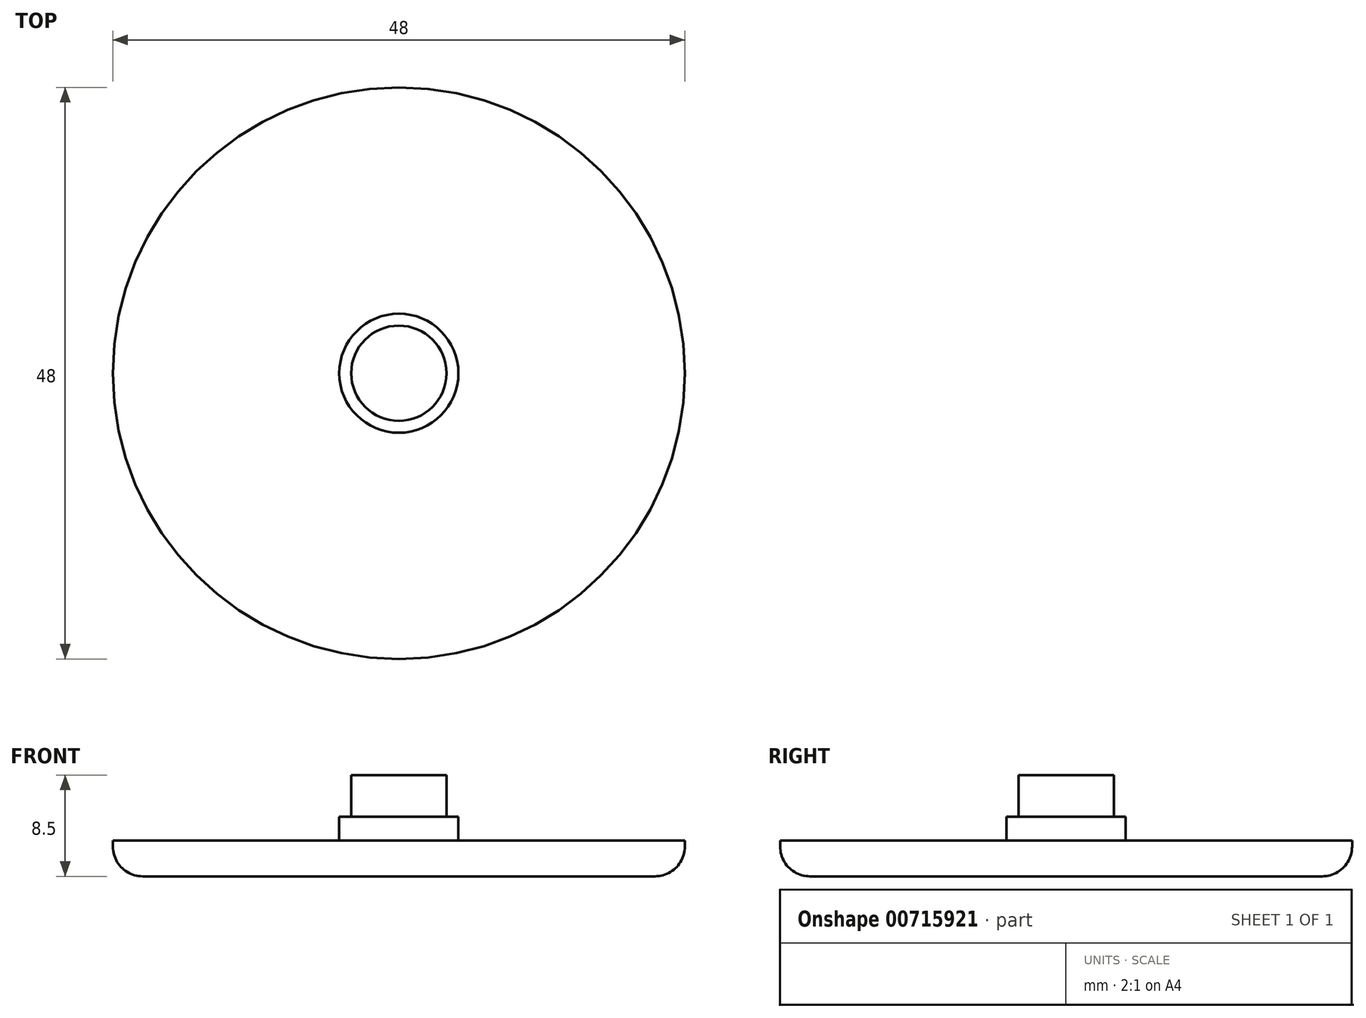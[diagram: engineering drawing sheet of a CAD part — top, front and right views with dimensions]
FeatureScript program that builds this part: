
annotation { "Feature Type Name" : "Feature", "Feature Type Description" : "" }
export const myFeature = defineFeature(function(context is Context, id is Id, definition is map)
    precondition{}
    {
        {
            var Q0;
            Q0=qCreatedBy(makeId("Top.planeOp"),FACE);
            var sketch = newSketch(context, id + "F0", { "sketchPlane" : qUnion([Q0])});
            skCircle(sketch, "E0", {"center": v(0, 0) * mm, "radius": 4 * mm});
            skSolve(sketch);
        }
        {
            var Q0;
            Q0=qCreatedBy(makeId("Top.planeOp"),FACE);
            var sketch = newSketch(context, id + "F1", { "sketchPlane" : qUnion([Q0])});
            skCircle(sketch, "E1", {"center": v(0, 0) * mm, "radius": 5 * mm});
            skSolve(sketch);
        }
        {
            var Q0;
            Q0=qCreatedBy(makeId("Top.planeOp"),FACE);
            var sketch = newSketch(context, id + "F2", { "sketchPlane" : qUnion([Q0])});
            skCircle(sketch, "E2", {"center": v(0, 0) * mm, "radius": 24 * mm});
            skSolve(sketch);
        }
        {
            var Q0;
            Q0 = qSketchRegion(id + "F2", true);
            extrude(context, id + "F3", {"entities" : qUnion([Q0]), "depth" : 0 * mm, "offsetDistance" : 25 * mm, "hasSecondDirection" : true, "secondDirectionOppositeDirection" : true, "secondDirectionDepth" : 3 * mm});
        }
        {
            var Q0;
            Q0 = qSketchRegion(id + "F1", true);
            extrude(context, id + "F4", {"entities" : qUnion([Q0]), "operationType" : NewBodyOperationType.ADD, "depth" : 2 * mm, "offsetDistance" : 25 * mm});
        }
        {
            var Q0;
            Q0 = qSketchRegion(id + "F0", true);
            extrude(context, id + "F5", {"entities" : qUnion([Q0]), "operationType" : NewBodyOperationType.ADD, "depth" : 5.5 * mm, "offsetDistance" : 25 * mm});
        }
        {
            var Q0;
            Q0=makeQuery(id+"F3.opExtrude","CAP_EDGE",EDGE,{"disambiguationData":[OSD([sQuery(id+"F2.wireOp",EDGE,"E2")])],"isStart":true});
            fillet(context, id + "F6", {"entities" : qUnion([Q0]), "radius" : 2.5 * mm, "tangentPropagation" : true, "allowEdgeOverflow" : false});
        }
    });
